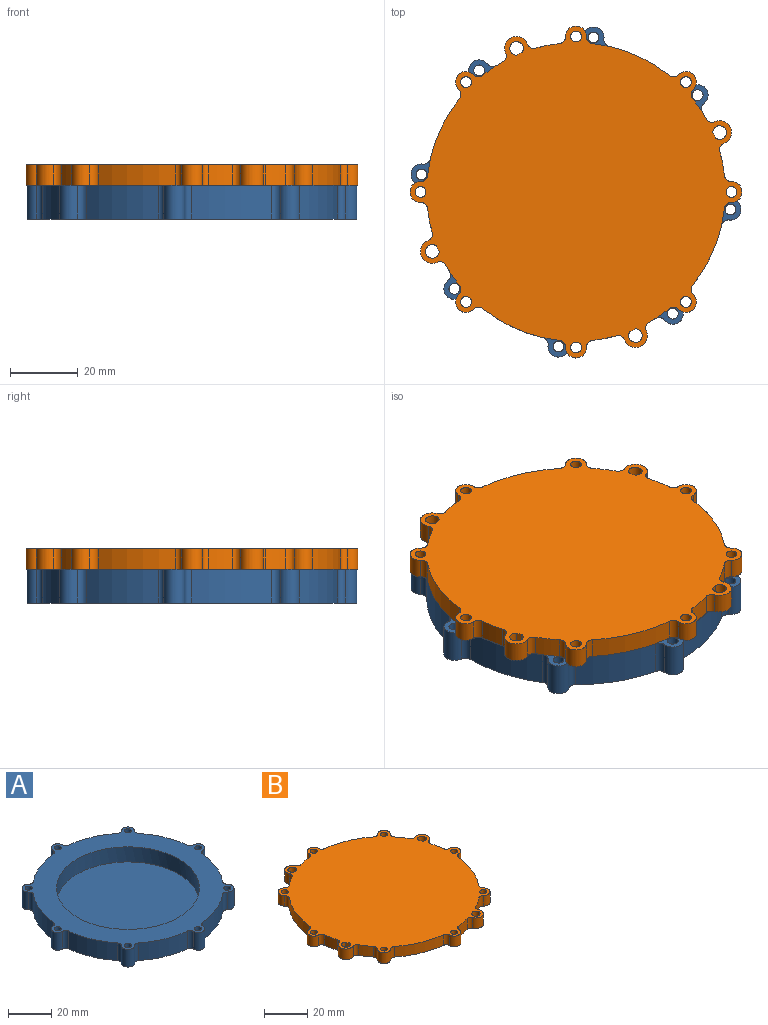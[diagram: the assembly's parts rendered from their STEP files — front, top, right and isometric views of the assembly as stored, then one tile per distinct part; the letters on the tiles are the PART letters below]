
ASSEMBLY  parts=2 mates=1
PART A: 94 faces, bbox 97.8x97.8x10 mm
  f0: cone r=39mm half-angle=5deg, axis (0,0,-1), area 287.6mm2, adj f14,f71,f87,f92
  f1: cone r=39mm half-angle=5deg, axis (0,0,-1), area 287.6mm2, adj f8,f15,f90,f93
  f2: cone r=39mm half-angle=5deg, axis (0,0,-1), area 287.6mm2, adj f9,f16,f88,f91
  f3: cone r=39mm half-angle=5deg, axis (0,0,-1), area 287.6mm2, adj f10,f17,f86,f89
  f4: cone r=38mm half-angle=5deg, axis (0,0,1), area 283.3mm2, adj f72,f73,f75,f83
  f5: cone r=38mm half-angle=5deg, axis (0,0,1), area 283.3mm2, adj f11,f18,f80,f84
  f6: cone r=38mm half-angle=5deg, axis (0,0,1), area 283.3mm2, adj f12,f19,f77,f81
  f7: cone r=38mm half-angle=5deg, axis (0,0,1), area 283.3mm2, adj f13,f20,f74,f78
  f8: torus R=38.52mm, axis (0,0,1), area 4.3mm2, adj f1,f33,f90,f93
  f9: torus R=38.52mm, axis (0,0,1), area 4.3mm2, adj f2,f33,f88,f91
  f10: torus R=38.52mm, axis (0,0,1), area 4.3mm2, adj f3,f33,f86,f89
  f11: torus R=38.48mm, axis (0,0,1), area 4.3mm2, adj f5,f33,f80,f84
  f12: torus R=38.48mm, axis (0,0,1), area 4.3mm2, adj f6,f33,f77,f81
  f13: torus R=38.48mm, axis (0,0,1), area 4.3mm2, adj f7,f33,f74,f78
  f14: torus R=39.09mm, axis (0,0,1), area 8.8mm2, adj f0,f32,f87,f92
  f15: torus R=39.09mm, axis (0,0,1), area 8.8mm2, adj f1,f32,f90,f93
  f16: torus R=39.09mm, axis (0,0,1), area 8.8mm2, adj f2,f32,f88,f91
  f17: torus R=39.09mm, axis (0,0,1), area 8.8mm2, adj f3,f32,f86,f89
  f18: torus R=37.91mm, axis (0,0,-1), area 8.6mm2, adj f5,f34,f80,f84
  f19: torus R=37.91mm, axis (0,0,-1), area 8.6mm2, adj f6,f34,f77,f81
  f20: torus R=37.91mm, axis (0,0,-1), area 8.6mm2, adj f7,f34,f74,f78
  f21: cylinder r=44mm len=22.59mm, axis (0,0,-1), area 247.8mm2, adj f31,f32,f35,f65
  f22: cylinder r=44mm len=22.59mm, axis (0,0,-1), area 247.8mm2, adj f31,f32,f61,f63
  f23: cylinder r=44mm len=22.59mm, axis (0,0,-1), area 247.8mm2, adj f31,f32,f57,f59
  f24: cylinder r=44mm len=22.59mm, axis (0,0,-1), area 247.8mm2, adj f31,f32,f53,f55
  f25: cylinder r=44mm len=22.59mm, axis (0,0,-1), area 247.8mm2, adj f31,f32,f49,f51
  f26: cylinder r=44mm len=22.59mm, axis (0,0,-1), area 247.8mm2, adj f31,f32,f45,f47
  f27: cylinder r=44mm len=22.59mm, axis (0,0,-1), area 247.8mm2, adj f31,f32,f41,f43
  f28: cylinder r=44mm len=22.59mm, axis (0,0,-1), area 247.8mm2, adj f31,f32,f37,f39
  f29: plane 66x66mm, normal (0,0,1), area 3421.2mm2, adj f30
  f30: cylinder r=33mm len=66mm, axis (0,0,-1), area 1762.4mm2, adj f29,f31
  f31: plane 97.8x97.8mm, normal (0,0,1), area 2819.3mm2, adj f21,f22,f23,f24,f25,f26,f27,f28
  f32: plane 97.8x97.8mm, normal (0,0,-1), area 1414.1mm2, adj f14,f15,f16,f17,f21,f22,f23,f24
  f33: plane 78.68x78.68mm, normal (0,0,-1), area 42.9mm2, adj f8,f9,f10,f11,f12,f13,f67,f68
  f34: plane 75.82x75.82mm, normal (0,0,-1), area 4514.6mm2, adj f18,f19,f20,f73,f76,f79,f82,f85
  f35: cylinder r=2mm len=10mm, axis (0,0,-1), area 29.5mm2, adj f21,f31,f32,f36
  f36: cylinder r=3.1mm len=10mm, axis (0,0,-1), area 98.4mm2, adj f31,f32,f35,f37
  f37: cylinder r=2mm len=10mm, axis (0,0,-1), area 29.5mm2, adj f28,f31,f32,f36
  f38: cylinder r=1.6mm len=10mm, axis (0,0,-1), area 100.5mm2, adj f31,f32
  f39: cylinder r=2mm len=10mm, axis (0,0,-1), area 29.5mm2, adj f28,f31,f32,f40
  f40: cylinder r=3.1mm len=10mm, axis (0,0,-1), area 98.4mm2, adj f31,f32,f39,f41
  f41: cylinder r=2mm len=10mm, axis (0,0,-1), area 29.5mm2, adj f27,f31,f32,f40
  f42: cylinder r=1.6mm len=10mm, axis (0,0,-1), area 100.5mm2, adj f31,f32
  f43: cylinder r=2mm len=10mm, axis (0,0,-1), area 29.5mm2, adj f27,f31,f32,f44
  f44: cylinder r=3.1mm len=10mm, axis (0,0,-1), area 98.4mm2, adj f31,f32,f43,f45
  f45: cylinder r=2mm len=10mm, axis (0,0,-1), area 29.5mm2, adj f26,f31,f32,f44
  f46: cylinder r=1.6mm len=10mm, axis (0,0,-1), area 100.5mm2, adj f31,f32
  f47: cylinder r=2mm len=10mm, axis (0,0,-1), area 29.5mm2, adj f26,f31,f32,f48
  f48: cylinder r=3.1mm len=10mm, axis (0,0,-1), area 98.4mm2, adj f31,f32,f47,f49
  f49: cylinder r=2mm len=10mm, axis (0,0,-1), area 29.5mm2, adj f25,f31,f32,f48
  f50: cylinder r=1.6mm len=10mm, axis (0,0,-1), area 100.5mm2, adj f31,f32
  f51: cylinder r=2mm len=10mm, axis (0,0,-1), area 29.5mm2, adj f25,f31,f32,f52
  f52: cylinder r=3.1mm len=10mm, axis (0,0,-1), area 98.4mm2, adj f31,f32,f51,f53
  f53: cylinder r=2mm len=10mm, axis (0,0,-1), area 29.5mm2, adj f24,f31,f32,f52
  f54: cylinder r=1.6mm len=10mm, axis (0,0,-1), area 100.5mm2, adj f31,f32
  f55: cylinder r=2mm len=10mm, axis (0,0,-1), area 29.5mm2, adj f24,f31,f32,f56
  f56: cylinder r=3.1mm len=10mm, axis (0,0,-1), area 98.4mm2, adj f31,f32,f55,f57
  f57: cylinder r=2mm len=10mm, axis (0,0,-1), area 29.5mm2, adj f23,f31,f32,f56
  f58: cylinder r=1.6mm len=10mm, axis (0,0,-1), area 100.5mm2, adj f31,f32
  f59: cylinder r=2mm len=10mm, axis (0,0,-1), area 29.5mm2, adj f23,f31,f32,f60
  f60: cylinder r=3.1mm len=10mm, axis (0,0,-1), area 98.4mm2, adj f31,f32,f59,f61
  f61: cylinder r=2mm len=10mm, axis (0,0,-1), area 29.5mm2, adj f22,f31,f32,f60
  f62: cylinder r=1.6mm len=10mm, axis (0,0,-1), area 100.5mm2, adj f31,f32
  f63: cylinder r=2mm len=10mm, axis (0,0,-1), area 29.5mm2, adj f22,f31,f32,f64
  f64: cylinder r=3.1mm len=10mm, axis (0,0,-1), area 98.4mm2, adj f31,f32,f63,f65
  f65: cylinder r=2mm len=10mm, axis (0,0,-1), area 29.5mm2, adj f21,f31,f32,f64
  f66: cylinder r=1.6mm len=10mm, axis (0,0,-1), area 100.5mm2, adj f31,f32
  f67: cylinder r=1mm len=5mm, axis (0,0,-1), area 15.7mm2, adj f32,f33,f86,f87
  f68: cylinder r=1mm len=5mm, axis (0,0,-1), area 15.7mm2, adj f32,f33,f90,f91
  f69: cylinder r=1mm len=5mm, axis (0,0,-1), area 15.7mm2, adj f32,f33,f88,f89
  f70: cylinder r=1mm len=5mm, axis (0,0,-1), area 15.7mm2, adj f32,f33,f92,f93
  f71: torus R=38.52mm, axis (0,0,1), area 4.3mm2, adj f0,f33,f87,f92
  f72: torus R=38.48mm, axis (0,0,1), area 4.3mm2, adj f4,f33,f75,f83
  f73: torus R=37.91mm, axis (0,0,-1), area 8.6mm2, adj f4,f34,f75,f83
  f74: plane 5x0.54mm, normal (0.36,0.93,0), area 1.6mm2, adj f7,f13,f20,f33,f76
  f75: plane 5x0.54mm, normal (-0.36,-0.93,0), area 1.6mm2, adj f4,f33,f72,f73,f76
  f76: cylinder r=37.91mm len=5mm, axis (0,0,-1), area 10mm2, adj f33,f34,f74,f75
  f77: plane 5x0.54mm, normal (-0.93,0.36,0), area 1.6mm2, adj f6,f12,f19,f33,f79
  f78: plane 5x0.54mm, normal (0.93,-0.36,0), area 1.6mm2, adj f7,f13,f20,f33,f79
  f79: cylinder r=37.91mm len=5mm, axis (0,0,-1), area 10mm2, adj f33,f34,f77,f78
  f80: plane 5x0.54mm, normal (-0.36,-0.93,0), area 1.6mm2, adj f5,f11,f18,f33,f82
  f81: plane 5x0.54mm, normal (0.36,0.93,0), area 1.6mm2, adj f6,f12,f19,f33,f82
  f82: cylinder r=37.91mm len=5mm, axis (0,0,-1), area 10mm2, adj f33,f34,f80,f81
  f83: plane 5x0.54mm, normal (0.93,-0.36,0), area 1.6mm2, adj f4,f33,f72,f73,f85
  f84: plane 5x0.54mm, normal (-0.93,0.36,0), area 1.6mm2, adj f5,f11,f18,f33,f85
  f85: cylinder r=37.91mm len=5mm, axis (0,0,-1), area 10mm2, adj f33,f34,f83,f84
  f86: plane 5x2.77mm, normal (0.36,0.93,0), area 13.5mm2, adj f3,f10,f17,f32,f33,f67
  f87: plane 5x2.82mm, normal (-0.36,-0.93,0), area 13.8mm2, adj f0,f14,f32,f33,f67,f71
  f88: plane 5x2.77mm, normal (-0.93,0.36,0), area 13.5mm2, adj f2,f9,f16,f32,f33,f69
  f89: plane 5x2.82mm, normal (0.93,-0.36,0), area 13.8mm2, adj f3,f10,f17,f32,f33,f69
  f90: plane 5x2.77mm, normal (-0.36,-0.93,0), area 13.5mm2, adj f1,f8,f15,f32,f33,f68
  f91: plane 5x2.82mm, normal (0.36,0.93,0), area 13.8mm2, adj f2,f9,f16,f32,f33,f68
  f92: plane 5x2.77mm, normal (0.93,-0.36,0), area 13.5mm2, adj f0,f14,f32,f33,f70,f71
  f93: plane 5x2.82mm, normal (-0.93,0.36,0), area 13.8mm2, adj f1,f8,f15,f32,f33,f70
PART B: 68 faces, bbox 97.8x97.8x6 mm
  f0: cylinder r=44mm len=6mm, axis (0,0,1), area 42.7mm2, adj f16,f17,f32,f67
  f1: cylinder r=44mm len=6mm, axis (0,0,1), area 10.3mm2, adj f16,f17,f64
  f2: cylinder r=44mm len=6mm, axis (0,0,1), area 42.7mm2, adj f16,f17,f24,f63
  f3: cylinder r=44mm len=6mm, axis (0,0,1), area 10.3mm2, adj f16,f17,f60
  f4: cylinder r=44mm len=6mm, axis (0,0,1), area 42.7mm2, adj f16,f17,f48,f59
  f5: cylinder r=44mm len=6mm, axis (0,0,1), area 10.3mm2, adj f16,f17,f56
  f6: cylinder r=44mm len=6mm, axis (0,0,1), area 42.7mm2, adj f16,f17,f40,f55
  f7: cylinder r=44mm len=6mm, axis (0,0,1), area 10.3mm2, adj f16,f17,f52
  f8: cylinder r=44mm len=22.59mm, axis (0,0,1), area 148.7mm2, adj f16,f17,f20,f50
  f9: cylinder r=44mm len=6.98mm, axis (0,0,1), area 42.7mm2, adj f16,f17,f46,f57
  f10: cylinder r=44mm len=22.59mm, axis (0,0,1), area 148.7mm2, adj f16,f17,f42,f44
  f11: cylinder r=44mm len=6.98mm, axis (0,0,1), area 42.7mm2, adj f16,f17,f38,f53
  f12: cylinder r=44mm len=22.59mm, axis (0,0,1), area 148.7mm2, adj f16,f17,f34,f36
  f13: cylinder r=44mm len=6.98mm, axis (0,0,1), area 42.7mm2, adj f16,f17,f30,f65
  f14: cylinder r=44mm len=22.59mm, axis (0,0,1), area 148.7mm2, adj f16,f17,f26,f28
  f15: cylinder r=44mm len=6.98mm, axis (0,0,1), area 42.7mm2, adj f16,f17,f22,f61
  f16: plane 97.8x97.8mm, normal (0,0,1), area 6325.1mm2, adj f0,f1,f2,f3,f4,f5,f6,f7
  f17: plane 97.8x97.8mm, normal (0,0,-1), area 1546.8mm2, adj f0,f1,f2,f3,f4,f5,f6,f7
  f18: cylinder r=39mm len=78mm, axis (0,0,-1), area 245mm2, adj f17,f19
  f19: plane 78x78mm, normal (0,0,-1), area 4778.4mm2, adj f18
  f20: cylinder r=2mm len=6mm, axis (0,0,1), area 17.7mm2, adj f8,f16,f17,f21
  f21: cylinder r=3.1mm len=6.2mm, axis (0,0,1), area 59mm2, adj f16,f17,f20,f22
  f22: cylinder r=2mm len=6mm, axis (0,0,1), area 17.7mm2, adj f15,f16,f17,f21
  f23: cylinder r=1.6mm len=6mm, axis (0,0,1), area 60.3mm2, adj f16,f17
  f24: cylinder r=2mm len=6mm, axis (0,0,1), area 17.7mm2, adj f2,f16,f17,f25
  f25: cylinder r=3.1mm len=6mm, axis (0,0,1), area 59mm2, adj f16,f17,f24,f26
  f26: cylinder r=2mm len=6mm, axis (0,0,1), area 17.7mm2, adj f14,f16,f17,f25
  f27: cylinder r=1.6mm len=6mm, axis (0,0,1), area 60.3mm2, adj f16,f17
  f28: cylinder r=2mm len=6mm, axis (0,0,1), area 17.7mm2, adj f14,f16,f17,f29
  f29: cylinder r=3.1mm len=6.2mm, axis (0,0,1), area 59mm2, adj f16,f17,f28,f30
  f30: cylinder r=2mm len=6mm, axis (0,0,1), area 17.7mm2, adj f13,f16,f17,f29
  f31: cylinder r=1.6mm len=6mm, axis (0,0,1), area 60.3mm2, adj f16,f17
  f32: cylinder r=2mm len=6mm, axis (0,0,1), area 17.7mm2, adj f0,f16,f17,f33
  f33: cylinder r=3.1mm len=6mm, axis (0,0,1), area 59mm2, adj f16,f17,f32,f34
  f34: cylinder r=2mm len=6mm, axis (0,0,1), area 17.7mm2, adj f12,f16,f17,f33
  f35: cylinder r=1.6mm len=6mm, axis (0,0,1), area 60.3mm2, adj f16,f17
  f36: cylinder r=2mm len=6mm, axis (0,0,1), area 17.7mm2, adj f12,f16,f17,f37
  f37: cylinder r=3.1mm len=6.2mm, axis (0,0,1), area 59mm2, adj f16,f17,f36,f38
  f38: cylinder r=2mm len=6mm, axis (0,0,1), area 17.7mm2, adj f11,f16,f17,f37
  f39: cylinder r=1.6mm len=6mm, axis (0,0,1), area 60.3mm2, adj f16,f17
  f40: cylinder r=2mm len=6mm, axis (0,0,1), area 17.7mm2, adj f6,f16,f17,f41
  f41: cylinder r=3.1mm len=6mm, axis (0,0,1), area 59mm2, adj f16,f17,f40,f42
  f42: cylinder r=2mm len=6mm, axis (0,0,1), area 17.7mm2, adj f10,f16,f17,f41
  f43: cylinder r=1.6mm len=6mm, axis (0,0,1), area 60.3mm2, adj f16,f17
  f44: cylinder r=2mm len=6mm, axis (0,0,1), area 17.7mm2, adj f10,f16,f17,f45
  f45: cylinder r=3.1mm len=6.2mm, axis (0,0,1), area 59mm2, adj f16,f17,f44,f46
  f46: cylinder r=2mm len=6mm, axis (0,0,1), area 17.7mm2, adj f9,f16,f17,f45
  f47: cylinder r=1.6mm len=6mm, axis (0,0,1), area 60.3mm2, adj f16,f17
  f48: cylinder r=2mm len=6mm, axis (0,0,1), area 17.7mm2, adj f4,f16,f17,f49
  f49: cylinder r=3.1mm len=6mm, axis (0,0,1), area 59mm2, adj f16,f17,f48,f50
  f50: cylinder r=2mm len=6mm, axis (0,0,1), area 17.7mm2, adj f8,f16,f17,f49
  f51: cylinder r=1.6mm len=6mm, axis (0,0,1), area 60.3mm2, adj f16,f17
  f52: cylinder r=2mm len=6mm, axis (0,0,1), area 64.8mm2, adj f7,f16,f17
  f53: cylinder r=2mm len=6mm, axis (0,0,1), area 17.7mm2, adj f11,f16,f17,f54
  f54: cylinder r=3.5mm len=6.76mm, axis (0,0,1), area 67mm2, adj f16,f17,f53,f55
  f55: cylinder r=2mm len=6mm, axis (0,0,1), area 17.7mm2, adj f6,f16,f17,f54
  f56: cylinder r=2mm len=6mm, axis (0,0,1), area 64.8mm2, adj f5,f16,f17
  f57: cylinder r=2mm len=6mm, axis (0,0,1), area 17.7mm2, adj f9,f16,f17,f58
  f58: cylinder r=3.5mm len=6.76mm, axis (0,0,1), area 67mm2, adj f16,f17,f57,f59
  f59: cylinder r=2mm len=6mm, axis (0,0,1), area 17.7mm2, adj f4,f16,f17,f58
  f60: cylinder r=2mm len=6mm, axis (0,0,1), area 64.8mm2, adj f3,f16,f17
  f61: cylinder r=2mm len=6mm, axis (0,0,1), area 17.7mm2, adj f15,f16,f17,f62
  f62: cylinder r=3.5mm len=6.76mm, axis (0,0,1), area 67mm2, adj f16,f17,f61,f63
  f63: cylinder r=2mm len=6mm, axis (0,0,1), area 17.7mm2, adj f2,f16,f17,f62
  f64: cylinder r=2mm len=6mm, axis (0,0,1), area 64.8mm2, adj f1,f16,f17
  f65: cylinder r=2mm len=6mm, axis (0,0,1), area 17.7mm2, adj f13,f16,f17,f66
  f66: cylinder r=3.5mm len=6.76mm, axis (0,0,1), area 67mm2, adj f16,f17,f65,f67
  f67: cylinder r=2mm len=6mm, axis (0,0,1), area 17.7mm2, adj f0,f16,f17,f66
PLACE A rot(axis=(0.9,-0.43,0),180deg) t=(-0.24,-11.18,-17.94)mm
PLACE B t=(-0.24,-11.18,-12.94)mm fixed
MATE planar A.f0 <-> B.f18  axis (0,0,1) through (-0.24,-11.18,-12.94)mm
